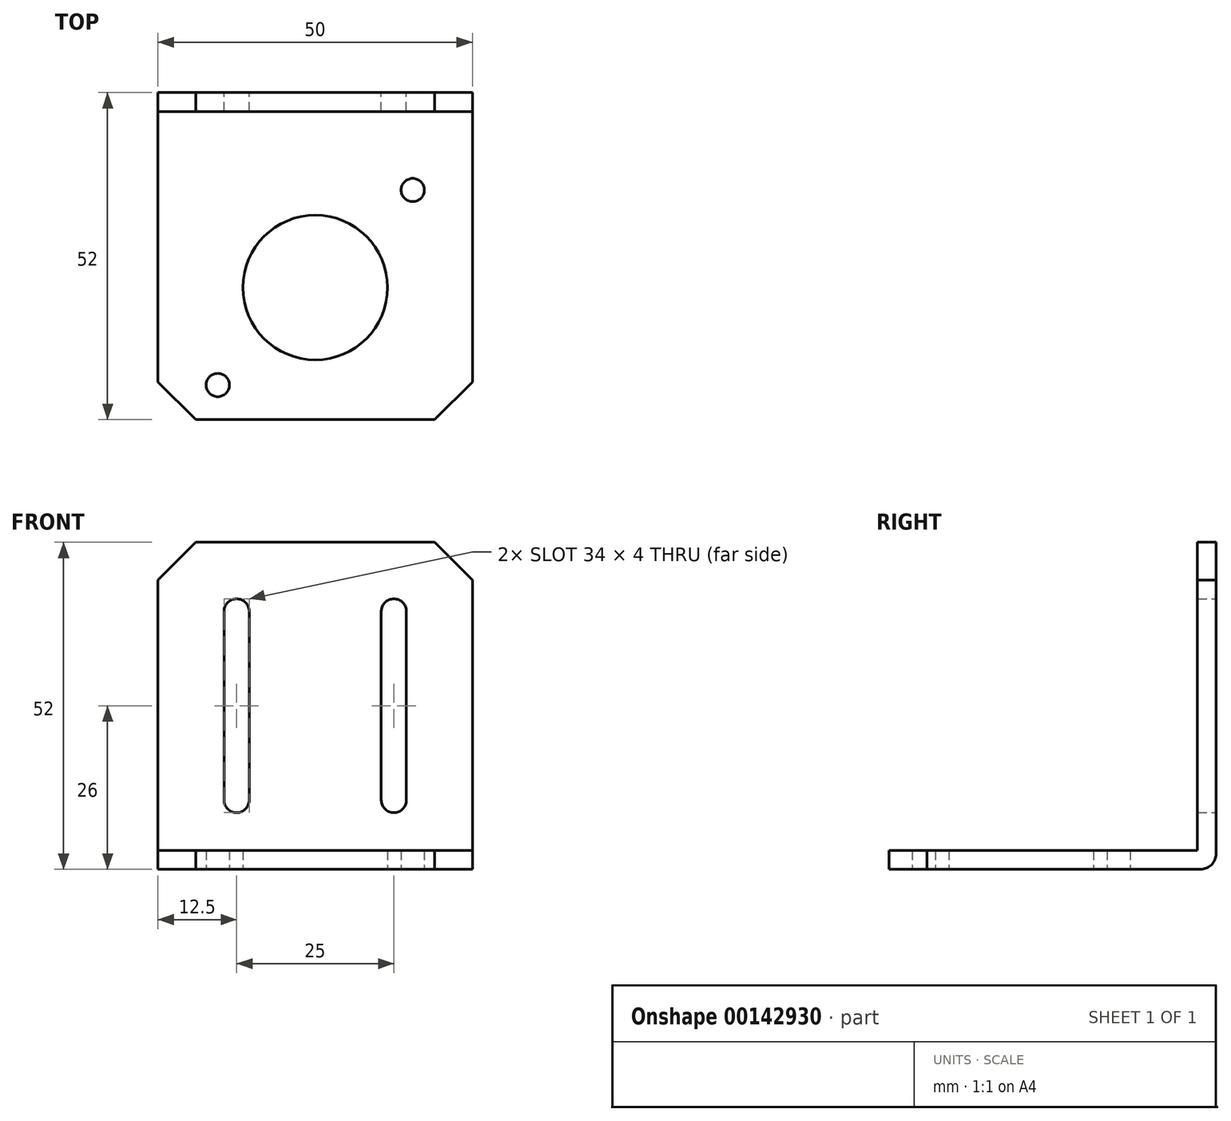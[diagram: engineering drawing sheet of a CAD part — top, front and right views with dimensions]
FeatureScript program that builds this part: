
annotation { "Feature Type Name" : "Feature", "Feature Type Description" : "" }
export const myFeature = defineFeature(function(context is Context, id is Id, definition is map)
    precondition{}
    {
        {
            var Q0;
            Q0=qCreatedBy(makeId("Right.planeOp"),FACE);
            var sketch = newSketch(context, id + "F0", { "sketchPlane" : qUnion([Q0])});
            skLineSegment(sketch, "E0", {"start": v(-52, 0) * mm, "end": v(-2.5, 0) * mm});
            skLineSegment(sketch, "E1", {"start": v(0, 2.5) * mm, "end": v(0, 52) * mm});
            skLineSegment(sketch, "E2.0", {"start": v(-3, 3) * mm, "end": v(-3, 52) * mm});
            skLineSegment(sketch, "E2.1", {"start": v(-52, 3) * mm, "end": v(-3, 3) * mm});
            skLineSegment(sketch, "E3", {"start": v(-52, 3) * mm, "end": v(-52, 0) * mm});
            skLineSegment(sketch, "E4", {"start": v(-3, 52) * mm, "end": v(0, 52) * mm});
            skPoint(sketch, "E5.visualSharp", {"position": v(0, 0) * mm});
            skArc(sketch, "E5.filletArc", {"start": v(-2.5, 0) * mm, "mid": v(-0.73, 0.73) * mm, "end": v(0, 2.5) * mm});
            skSolve(sketch);
        }
        {
            var Q0;
            Q0 = qSketchRegion(id + "F0", true);
            extrude(context, id + "F1", {"entities" : qUnion([Q0]), "oppositeDirection" : true, "depth" : 50 * mm});
        }
        {
            var Q0;
            Q0=qCreatedBy(makeId("Top.planeOp"),FACE);
            var sketch = newSketch(context, id + "F2", { "sketchPlane" : qUnion([Q0])});
            skCircle(sketch, "E6", {"center": v(-25, -31) * mm, "radius": 11.5 * mm});
            skCircle(sketch, "E7", {"center": v(-40.5, -46.5) * mm, "radius": 1.85 * mm});
            skLineSegment(sketch, "E8", {"start": v(-25, -31) * mm, "end": v(-25, -58.4) * mm, "construction": true});
            skCircle(sketch, "E9.MirrorC", {"center": v(-9.5, -46.5) * mm, "radius": 1.85 * mm});
            skLineSegment(sketch, "E10", {"start": v(-25, -31) * mm, "end": v(-53.47, -31) * mm, "construction": true});
            skCircle(sketch, "E11.MirrorC", {"center": v(-40.5, -15.5) * mm, "radius": 1.85 * mm});
            skCircle(sketch, "E12.MirrorC", {"center": v(-9.5, -15.5) * mm, "radius": 1.85 * mm});
            skSolve(sketch);
        }
        {
            var Q0;
            Q0=makeQuery(id+"F2.imprint","IMPRINT",FACE,{"disambiguationData":[TD([[makeQuery(id+"F2.imprint","IMPRINT",EDGE,{"derivedFrom":sQuery(id+"F2.wireOp",EDGE,"E6")}),1.0]])]});
            var Q1;
            Q1=makeQuery(id+"F2.imprint","IMPRINT",FACE,{"disambiguationData":[TD([[makeQuery(id+"F2.imprint","IMPRINT",EDGE,{"derivedFrom":sQuery(id+"F2.wireOp",EDGE,"E9.MirrorC")}),-1.0]])]});
            var Q2;
            Q2=makeQuery(id+"F2.imprint","IMPRINT",FACE,{"disambiguationData":[TD([[makeQuery(id+"F2.imprint","IMPRINT",EDGE,{"derivedFrom":sQuery(id+"F2.wireOp",EDGE,"E12.MirrorC")}),1.0]])]});
            var Q3;
            Q3=makeQuery(id+"F2.imprint","IMPRINT",FACE,{"disambiguationData":[TD([[makeQuery(id+"F2.imprint","IMPRINT",EDGE,{"derivedFrom":sQuery(id+"F2.wireOp",EDGE,"E7")}),1.0]])]});
            var Q4;
            Q4=makeQuery(id+"F2.imprint","IMPRINT",FACE,{"disambiguationData":[TD([[makeQuery(id+"F2.imprint","IMPRINT",EDGE,{"derivedFrom":sQuery(id+"F2.wireOp",EDGE,"E11.MirrorC")}),-1.0]])]});
            extrude(context, id + "F3", {"entities" : qUnion([Q0, Q1, Q2, Q3, Q4]), "operationType" : NewBodyOperationType.REMOVE, "depth" : 3 * mm});
        }
        {
            var Q0;
            Q0=makeQuery(id+"F1.opExtrude","CAP_EDGE",EDGE,{"disambiguationData":[OSD([sQuery(id+"F0.wireOp",EDGE,"E3")])],"isStart":true});
            var Q1;
            Q1=makeQuery(id+"F1.opExtrude","CAP_EDGE",EDGE,{"disambiguationData":[OSD([sQuery(id+"F0.wireOp",EDGE,"E3")])],"isStart":false});
            var Q2;
            Q2=makeQuery(id+"F1.opExtrude","CAP_EDGE",EDGE,{"disambiguationData":[OSD([sQuery(id+"F0.wireOp",EDGE,"E4")])],"isStart":true});
            var Q3;
            Q3=makeQuery(id+"F1.opExtrude","CAP_EDGE",EDGE,{"disambiguationData":[OSD([sQuery(id+"F0.wireOp",EDGE,"E4")])],"isStart":false});
            chamfer(context, id + "F4", {"entities" : qUnion([Q0, Q1, Q2, Q3]), "width" : 6 * mm, "tangentPropagation" : true});
        }
        {
            var Q0;
            Q0=makeQuery(id+"F1.opExtrude","SWEPT_FACE",FACE,{"disambiguationData":[OSD([sQuery(id+"F0.wireOp",EDGE,"E1")])]});
            var sketch = newSketch(context, id + "F5", { "sketchPlane" : qUnion([Q0])});
            skArc(sketch, "E13", {"start": v(39.5, 41) * mm, "mid": v(37.5, 43) * mm, "end": v(35.5, 41) * mm});
            skArc(sketch, "E14", {"start": v(35.5, 11) * mm, "mid": v(37.5, 9) * mm, "end": v(39.5, 11) * mm});
            skLineSegment(sketch, "E15", {"start": v(35.5, 41) * mm, "end": v(35.5, 11) * mm});
            skLineSegment(sketch, "E16", {"start": v(39.5, 41) * mm, "end": v(39.5, 11) * mm});
            skLineSegment(sketch, "E17", {"start": v(25, 52) * mm, "end": v(25, 2.5) * mm, "construction": true});
            skLineSegment(sketch, "E18.MirrorCS", {"start": v(10.5, 41) * mm, "end": v(10.5, 11) * mm});
            skLineSegment(sketch, "E19.MirrorCS", {"start": v(14.5, 41) * mm, "end": v(14.5, 11) * mm});
            skArc(sketch, "E20.MirrorCS", {"start": v(14.5, 11) * mm, "mid": v(12.5, 9) * mm, "end": v(10.5, 11) * mm});
            skArc(sketch, "E21.MirrorCS", {"start": v(10.5, 41) * mm, "mid": v(12.5, 43) * mm, "end": v(14.5, 41) * mm});
            skSolve(sketch);
        }
        {
            var Q0;
            Q0=makeQuery(id+"F5.imprint","IMPRINT",FACE,{"disambiguationData":[TD([[makeQuery(id+"F5.imprint","IMPRINT",EDGE,{"derivedFrom":sQuery(id+"F5.wireOp",EDGE,"E13")}),1.0]])]});
            var Q1;
            Q1=makeQuery(id+"F5.imprint","IMPRINT",FACE,{"disambiguationData":[TD([[makeQuery(id+"F5.imprint","IMPRINT",EDGE,{"derivedFrom":sQuery(id+"F5.wireOp",EDGE,"E18.MirrorCS")}),1.0]])]});
            extrude(context, id + "F6", {"entities" : qUnion([Q0, Q1]), "operationType" : NewBodyOperationType.REMOVE, "oppositeDirection" : true, "depth" : 3 * mm});
        }
    });
